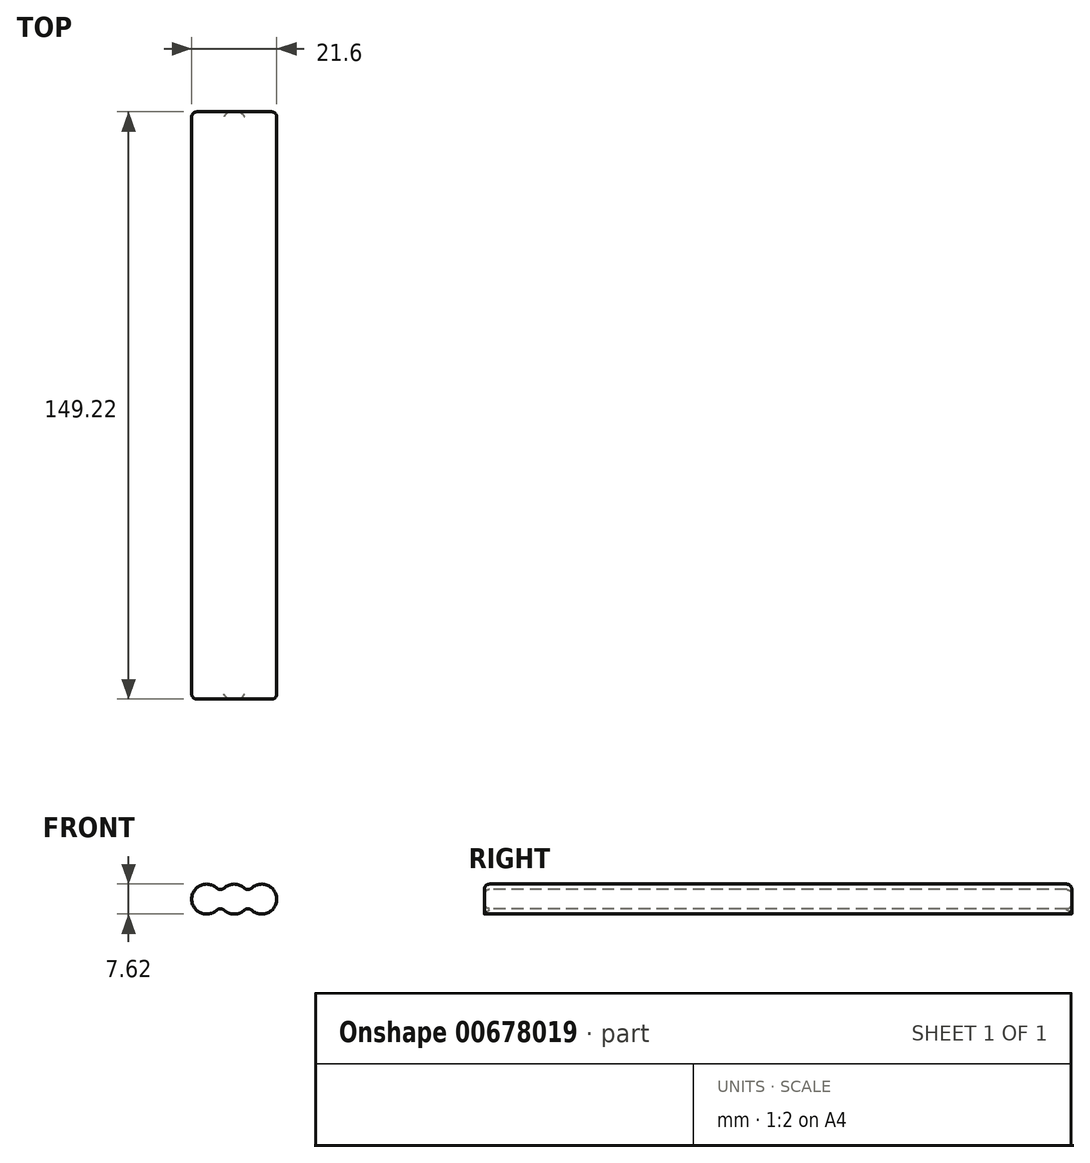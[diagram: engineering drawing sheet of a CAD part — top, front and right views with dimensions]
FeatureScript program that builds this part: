
annotation { "Feature Type Name" : "Feature", "Feature Type Description" : "" }
export const myFeature = defineFeature(function(context is Context, id is Id, definition is map)
    precondition{}
    {
        {
            var Q0;
            Q0=qCreatedBy(makeId("Front.planeOp"),FACE);
            var sketch = newSketch(context, id + "F0", { "sketchPlane" : qUnion([Q0])});
            skLineSegment(sketch, "E0", {"start": v(-6.99, 0) * mm, "end": v(6.99, 0) * mm, "construction": true});
            skArc(sketch, "E1", {"start": v(3.5, -1.52) * mm, "mid": v(10.8, 0) * mm, "end": v(3.5, 1.52) * mm});
            skArc(sketch, "E2", {"start": v(3.5, 1.52) * mm, "mid": v(0, 3.81) * mm, "end": v(-3.5, 1.52) * mm});
            skArc(sketch, "E3", {"start": v(-3.5, 1.52) * mm, "mid": v(-10.8, 0) * mm, "end": v(-3.5, -1.52) * mm});
            skArc(sketch, "E4.trimOffspring", {"start": v(-3.5, -1.52) * mm, "mid": v(0, -3.81) * mm, "end": v(3.5, -1.52) * mm});
            skSolve(sketch);
        }
        {
            var Q0;
            Q0=makeQuery(id+"F0.imprint","IMPRINT",FACE,{"disambiguationData":[TD([[makeQuery(id+"F0.imprint","IMPRINT",EDGE,{"derivedFrom":sQuery(id+"F0.wireOp",EDGE,"E1")}),1.0]])]});
            extrude(context, id + "F1", {"entities" : qUnion([Q0]), "endBound" : BoundingType.SYMMETRIC, "depth" : 149.22 * mm, "offsetDistance" : 25.4 * mm});
        }
        {
            var Q0;
            Q0=makeQuery(id+"F1.opExtrude","SWEPT_FACE",FACE,{"disambiguationData":[OSD([sQuery(id+"F0.wireOp",EDGE,"E2")])]});
            var Q1;
            Q1=makeQuery(id+"F1.opExtrude","SWEPT_FACE",FACE,{"disambiguationData":[OSD([sQuery(id+"F0.wireOp",EDGE,"E1")])]});
            var Q2;
            Q2=makeQuery(id+"F1.opExtrude","SWEPT_FACE",FACE,{"disambiguationData":[OSD([sQuery(id+"F0.wireOp",EDGE,"E3")])]});
            fillet(context, id + "F2", {"entities" : qUnion([Q0, Q1, Q2]), "radius" : 1.27 * mm, "tangentPropagation" : true, "allowEdgeOverflow" : false});
        }
    });
